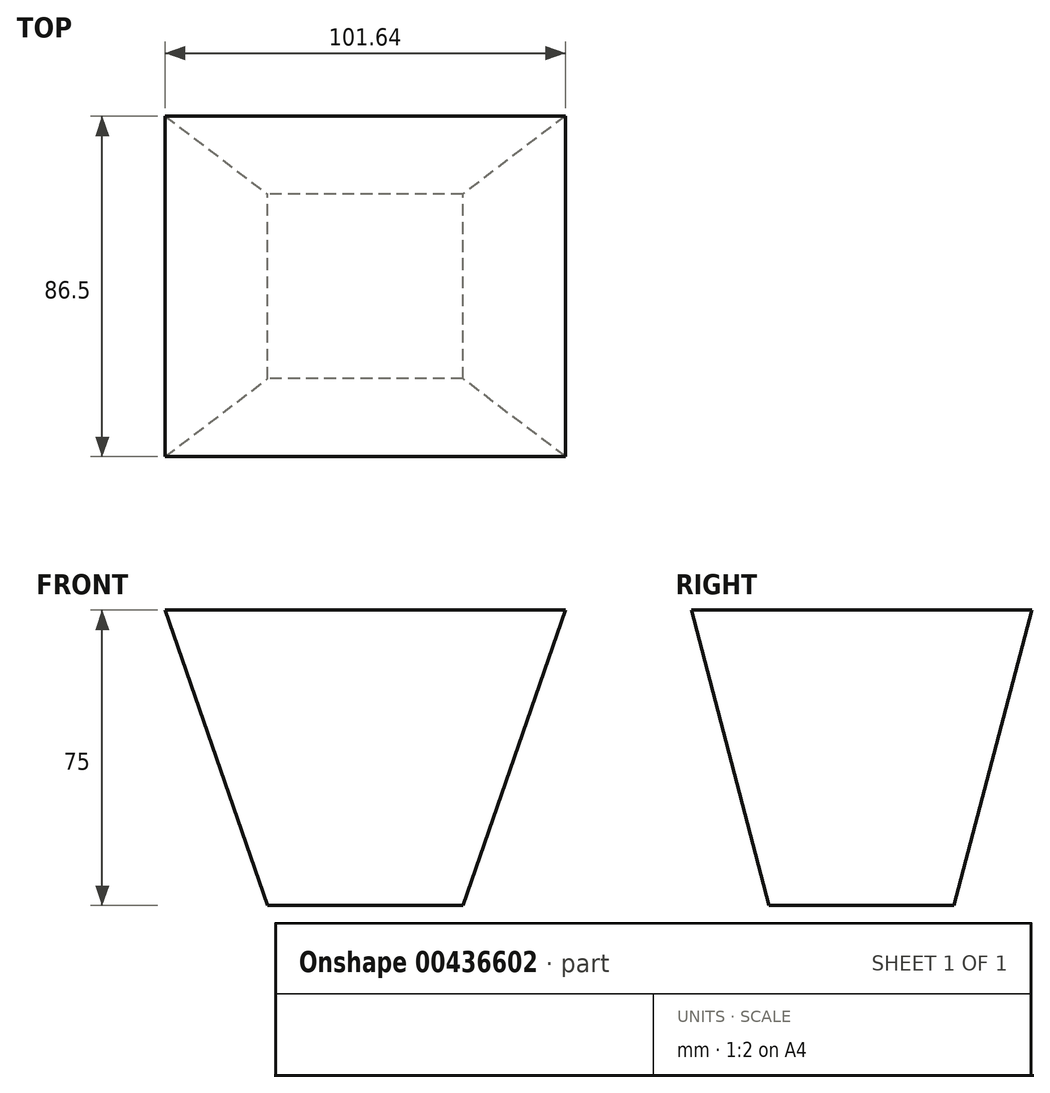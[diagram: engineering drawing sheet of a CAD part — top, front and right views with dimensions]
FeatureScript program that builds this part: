
annotation { "Feature Type Name" : "Feature", "Feature Type Description" : "" }
export const myFeature = defineFeature(function(context is Context, id is Id, definition is map)
    precondition{}
    {
        {
            var Q0;
            Q0=qCreatedBy(makeId("Top.planeOp"),FACE);
            var sketch = newSketch(context, id + "F0", { "sketchPlane" : qUnion([Q0])});
            skLineSegment(sketch, "E0.bottom", {"start": v(50.82, -43.25) * mm, "end": v(-50.82, -43.25) * mm});
            skLineSegment(sketch, "E0.top", {"start": v(50.82, 43.25) * mm, "end": v(-50.82, 43.25) * mm});
            skLineSegment(sketch, "E0.left", {"start": v(50.82, -43.25) * mm, "end": v(50.82, 43.25) * mm});
            skLineSegment(sketch, "E0.right", {"start": v(-50.82, -43.25) * mm, "end": v(-50.82, 43.25) * mm});
            skPoint(sketch, "E0.middle", {"position": v(0, 0) * mm});
            skSolve(sketch);
        }
        {
            var Q0;
            Q0=qCreatedBy(makeId("Top.planeOp"),FACE);
            cPlane(context, id + "F1", {"entities" : qUnion([Q0]), "cplaneType" : CPlaneType.OFFSET, "offset" : 75 * mm, "oppositeDirection" : true, "width" : 150 * mm, "height" : 150 * mm});
        }
        {
            var Q0;
            Q0=qCreatedBy(id+"F1.planeOp",FACE);
            var sketch = newSketch(context, id + "F2", { "sketchPlane" : qUnion([Q0])});
            skLineSegment(sketch, "E1.bottom", {"start": v(24.8, -23.45) * mm, "end": v(-24.8, -23.45) * mm});
            skLineSegment(sketch, "E1.top", {"start": v(24.8, 23.45) * mm, "end": v(-24.8, 23.45) * mm});
            skLineSegment(sketch, "E1.left", {"start": v(24.8, -23.45) * mm, "end": v(24.8, 23.45) * mm});
            skLineSegment(sketch, "E1.right", {"start": v(-24.8, -23.45) * mm, "end": v(-24.8, 23.45) * mm});
            skPoint(sketch, "E1.middle", {"position": v(0, 0) * mm});
            skSolve(sketch);
        }
        {
            var Q0;
            Q0=makeQuery(id+"F0.imprint","IMPRINT",FACE,{"disambiguationData":[TD([[makeQuery(id+"F0.imprint","IMPRINT",EDGE,{"derivedFrom":sQuery(id+"F0.wireOp",EDGE,"E0.bottom")}),-1.0]])]});
            var Q1;
            Q1=makeQuery(id+"F2.imprint","IMPRINT",FACE,{"disambiguationData":[TD([[makeQuery(id+"F2.imprint","IMPRINT",EDGE,{"derivedFrom":sQuery(id+"F2.wireOp",EDGE,"E1.bottom")}),-1.0]])]});
            loft(context, id + "F3", {"sheetProfilesArray" : [{ "sheetProfileEntities" : qUnion([Q0]) }, { "sheetProfileEntities" : qUnion([Q1]) }]});
        }
    });
